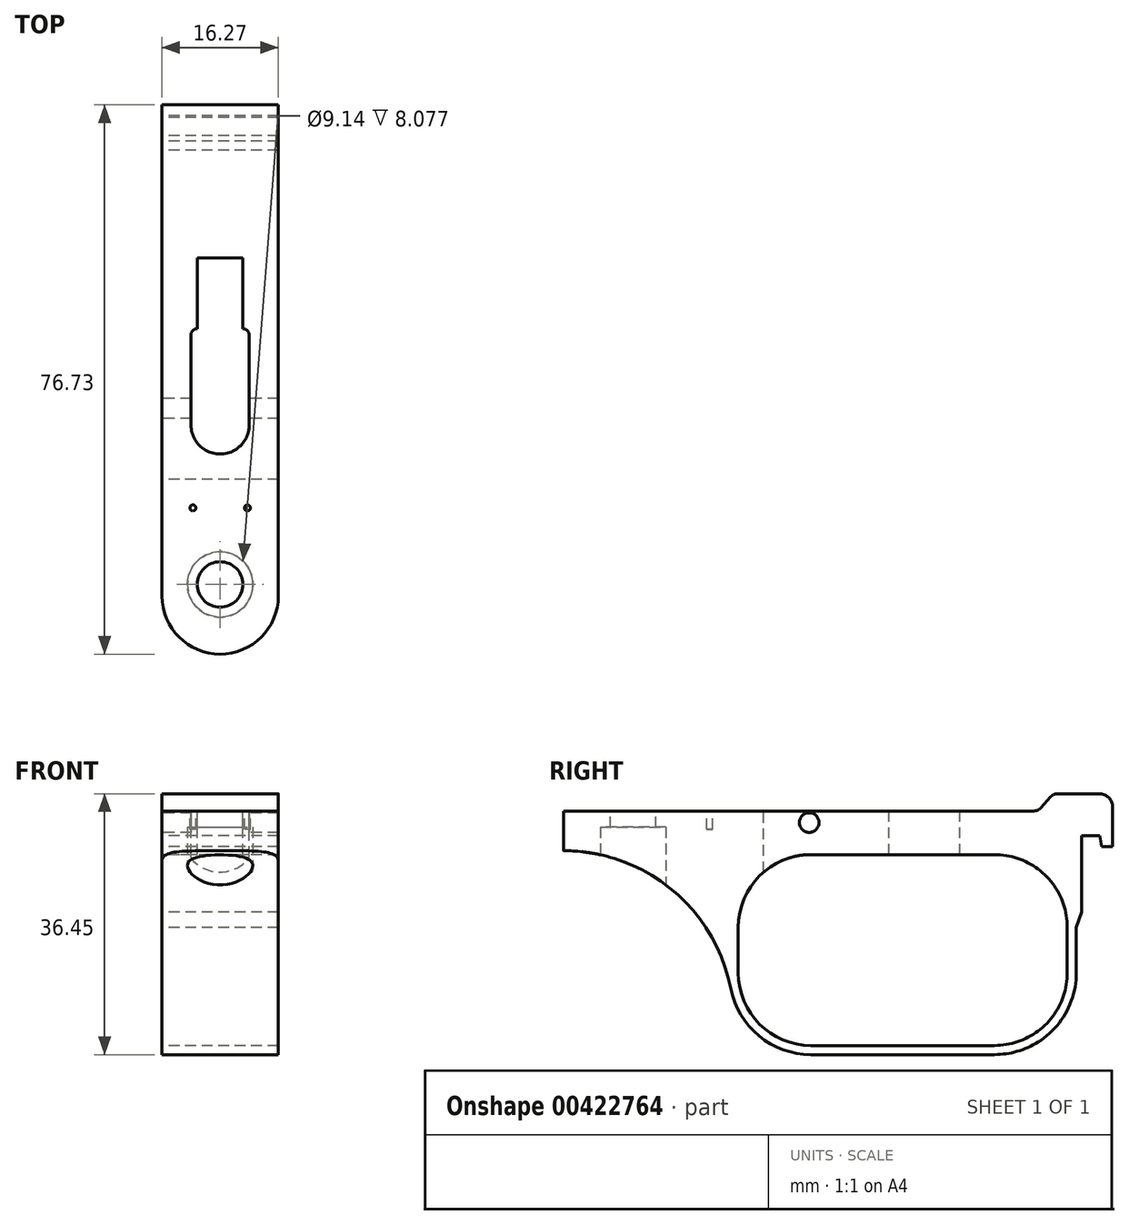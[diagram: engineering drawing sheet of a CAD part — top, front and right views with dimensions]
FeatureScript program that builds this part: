
annotation { "Feature Type Name" : "Feature", "Feature Type Description" : "" }
export const myFeature = defineFeature(function(context is Context, id is Id, definition is map)
    precondition{}
    {
        {
            var Q0;
            Q0=qCreatedBy(makeId("Top.planeOp"),FACE);
            var sketch = newSketch(context, id + "F0", { "sketchPlane" : qUnion([Q0])});
            skArc(sketch, "E0", {"start": v(-8.13, -41.11) * mm, "mid": v(0, -49.24) * mm, "end": v(8.13, -41.11) * mm});
            skCircle(sketch, "E1", {"center": v(0, -39.51) * mm, "radius": 3.18 * mm});
            skLineSegment(sketch, "E2", {"start": v(-8.13, -31.26) * mm, "end": v(8.13, -31.26) * mm});
            skCircle(sketch, "E3", {"center": v(3.81, -28.82) * mm, "radius": 0.42 * mm});
            skCircle(sketch, "E4", {"center": v(-3.8, -28.82) * mm, "radius": 0.42 * mm});
            skLineSegment(sketch, "E5", {"start": v(-8.13, -41.11) * mm, "end": v(-8.13, -31.26) * mm});
            skLineSegment(sketch, "E6", {"start": v(8.13, -41.11) * mm, "end": v(8.13, -31.26) * mm});
            skLineSegment(sketch, "E7", {"start": v(8.13, 17.06) * mm, "end": v(8.13, -31.26) * mm});
            skLineSegment(sketch, "E8", {"start": v(8.13, 17.06) * mm, "end": v(8.14, 23.18) * mm});
            skLineSegment(sketch, "E9", {"start": v(8.14, 23.18) * mm, "end": v(8.14, 25.72) * mm});
            skLineSegment(sketch, "E10", {"start": v(8.14, 25.72) * mm, "end": v(8.14, 27.5) * mm});
            skLineSegment(sketch, "E11", {"start": v(8.13, 17.06) * mm, "end": v(-8.13, 17.1) * mm});
            skLineSegment(sketch, "E12", {"start": v(8.14, 23.18) * mm, "end": v(-8.13, 23.18) * mm});
            skLineSegment(sketch, "E13", {"start": v(8.14, 25.72) * mm, "end": v(-8.13, 25.72) * mm});
            skLineSegment(sketch, "E14", {"start": v(8.14, 27.5) * mm, "end": v(-8.13, 27.5) * mm});
            skLineSegment(sketch, "E15", {"start": v(-8.13, -31.26) * mm, "end": v(-8.13, 17.1) * mm});
            skLineSegment(sketch, "E16", {"start": v(-8.13, 17.1) * mm, "end": v(-8.13, 23.18) * mm});
            skLineSegment(sketch, "E17", {"start": v(-8.13, 23.18) * mm, "end": v(-8.13, 25.72) * mm});
            skLineSegment(sketch, "E18", {"start": v(-8.13, 25.72) * mm, "end": v(-8.13, 27.5) * mm});
            skArc(sketch, "E19.0.1.0", {"start": v(-4.06, -17.24) * mm, "mid": v(0, -21.3) * mm, "end": v(4.07, -17.23) * mm});
            skLineSegment(sketch, "E19.0.1.1", {"start": v(-4.07, -4.66) * mm, "end": v(-4.06, -17.24) * mm});
            skLineSegment(sketch, "E19.0.1.2", {"start": v(4.05, -4.66) * mm, "end": v(4.07, -17.23) * mm});
            skArc(sketch, "E19.0.1.3", {"start": v(-3.18, -3.77) * mm, "mid": v(-3.8, -4.03) * mm, "end": v(-4.07, -4.66) * mm});
            skLineSegment(sketch, "E19.0.1.4", {"start": v(-3.18, -3.77) * mm, "end": v(-3.18, 6.13) * mm});
            skArc(sketch, "E19.0.1.5", {"start": v(4.05, -4.66) * mm, "mid": v(3.8, -4.04) * mm, "end": v(3.17, -3.77) * mm});
            skLineSegment(sketch, "E19.0.1.6", {"start": v(3.17, -3.77) * mm, "end": v(3.17, 6.13) * mm});
            skLineSegment(sketch, "E19.0.1.7", {"start": v(3.17, 6.13) * mm, "end": v(-3.18, 6.13) * mm});
            skSolve(sketch);
        }
        {
            var Q0;
            Q0=makeQuery(id+"F0.imprint","IMPRINT",FACE,{"disambiguationData":[TD([[makeQuery(id+"F0.imprint","IMPRINT",EDGE,{"derivedFrom":sQuery(id+"F0.wireOp",EDGE,"E0")}),1.0]])]});
            var Q1;
            {var subQ0=sQuery(id+"F0.wireOp",EDGE,"787198dd-bca4-4525-862f-a25401c4d90f");Q1=makeQuery(id+"F0.imprint","IMPRINT",FACE,{"disambiguationData":[TD([[makeQuery(id+"F0.imprint","IMPRINT",EDGE,{"derivedFrom":subQ0}),-1.0]])]});}
            var Q2;
            {var subQ0=sQuery(id+"F0.wireOp",EDGE,"d4342492-76fe-4402-a7e5-8071a383ea67");Q2=makeQuery(id+"F0.imprint","IMPRINT",FACE,{"disambiguationData":[TD([[makeQuery(id+"F0.imprint","IMPRINT",EDGE,{"derivedFrom":subQ0}),1.0]])]});}
            var Q3;
            Q3=makeQuery(id+"F0.imprint","IMPRINT",FACE,{"disambiguationData":[TD([[makeQuery(id+"F0.imprint","IMPRINT",EDGE,{"derivedFrom":sQuery(id+"F0.wireOp",EDGE,"14f3fbc3-f7db-4fca-b2d8-4976d205a7d3")}),1.0]])]});
            var Q4;
            Q4=makeQuery(id+"F0.imprint","IMPRINT",FACE,{"disambiguationData":[TD([[makeQuery(id+"F0.imprint","IMPRINT",EDGE,{"derivedFrom":sQuery(id+"F0.wireOp",EDGE,"E1")}),1.0]])]});
            var Q5;
            Q5=makeQuery(id+"F0.imprint","IMPRINT",FACE,{"disambiguationData":[TD([[makeQuery(id+"F0.imprint","IMPRINT",EDGE,{"derivedFrom":sQuery(id+"F0.wireOp",EDGE,"14f3fbc3-f7db-4fca-b2d8-4976d205a7d3")}),-1.0]])]});
            var Q6;
            Q6=makeQuery(id+"F0.imprint","IMPRINT",FACE,{"disambiguationData":[TD([[makeQuery(id+"F0.imprint","IMPRINT",EDGE,{"derivedFrom":sQuery(id+"F0.wireOp",EDGE,"E4")}),1.0]])]});
            var Q7;
            Q7=makeQuery(id+"F0.imprint","IMPRINT",FACE,{"disambiguationData":[TD([[makeQuery(id+"F0.imprint","IMPRINT",EDGE,{"derivedFrom":sQuery(id+"F0.wireOp",EDGE,"E3")}),1.0]])]});
            var Q8;
            Q8=makeQuery(id+"F0.imprint","IMPRINT",FACE,{"disambiguationData":[TD([[makeQuery(id+"F0.imprint","IMPRINT",EDGE,{"derivedFrom":sQuery(id+"F0.wireOp",EDGE,"E8")}),1.0]])]});
            var Q9;
            Q9=makeQuery(id+"F0.imprint","IMPRINT",FACE,{"disambiguationData":[TD([[makeQuery(id+"F0.imprint","IMPRINT",EDGE,{"derivedFrom":sQuery(id+"F0.wireOp",EDGE,"E2")}),1.0]])]});
            var Q10;
            Q10=makeQuery(id+"F0.imprint","IMPRINT",FACE,{"disambiguationData":[TD([[makeQuery(id+"F0.imprint","IMPRINT",EDGE,{"derivedFrom":sQuery(id+"F0.wireOp",EDGE,"E19.0.1.0")}),1.0]])]});
            extrude(context, id + "F1", {"entities" : qUnion([Q0, Q1, Q2, Q3, Q4, Q5, Q6, Q7, Q8, Q9, Q10]), "oppositeDirection" : true, "depth" : 34.54 * mm, "offsetDistance" : 25.4 * mm});
        }
        {
            var Q0;
            Q0=makeQuery(id+"F0.imprint","IMPRINT",FACE,{"disambiguationData":[TD([[makeQuery(id+"F0.imprint","IMPRINT",EDGE,{"derivedFrom":sQuery(id+"F0.wireOp",EDGE,"E8")}),1.0]])]});
            var Q1;
            Q1=makeQuery(id+"F0.imprint","IMPRINT",FACE,{"disambiguationData":[TD([[makeQuery(id+"F0.imprint","IMPRINT",EDGE,{"derivedFrom":sQuery(id+"F0.wireOp",EDGE,"E9")}),1.0]])]});
            var Q2;
            Q2=makeQuery(id+"F0.imprint","IMPRINT",FACE,{"disambiguationData":[TD([[makeQuery(id+"F0.imprint","IMPRINT",EDGE,{"derivedFrom":sQuery(id+"F0.wireOp",EDGE,"E10")}),1.0]])]});
            extrude(context, id + "F2", {"entities" : qUnion([Q0, Q1, Q2]), "operationType" : NewBodyOperationType.ADD, "depth" : 2.41 * mm, "offsetDistance" : 25.4 * mm});
        }
        {
            var Q0;
            Q0=makeQuery(id+"F0.imprint","IMPRINT",FACE,{"disambiguationData":[TD([[makeQuery(id+"F0.imprint","IMPRINT",EDGE,{"derivedFrom":sQuery(id+"F0.wireOp",EDGE,"E10")}),1.0]])]});
            extrude(context, id + "F3", {"entities" : qUnion([Q0]), "operationType" : NewBodyOperationType.ADD, "oppositeDirection" : true, "depth" : 4.95 * mm, "offsetDistance" : 25.4 * mm});
        }
        {
            var Q0;
            Q0=makeQuery(id+"F0.imprint","IMPRINT",FACE,{"disambiguationData":[TD([[makeQuery(id+"F0.imprint","IMPRINT",EDGE,{"derivedFrom":sQuery(id+"F0.wireOp",EDGE,"d4342492-76fe-4402-a7e5-8071a383ea67")}),-1.0]])]});
            var Q1;
            Q1=makeQuery(id+"F0.imprint","IMPRINT",FACE,{"disambiguationData":[TD([[makeQuery(id+"F0.imprint","IMPRINT",EDGE,{"derivedFrom":sQuery(id+"F0.wireOp",EDGE,"E9")}),1.0]])]});
            extrude(context, id + "F4", {"entities" : qUnion([Q0, Q1]), "operationType" : NewBodyOperationType.ADD, "oppositeDirection" : true, "depth" : 3.43 * mm, "offsetDistance" : 25.4 * mm});
        }
        {
            var Q0;
            Q0=makeQuery(id+"F3.opExtrude","CAP_EDGE",EDGE,{"disambiguationData":[OSD([sQuery(id+"F0.wireOp",EDGE,"E13")])],"isStart":false});
            chamfer(context, id + "F5", {"entities" : qUnion([Q0]), "chamferType" : ChamferType.TWO_OFFSETS, "width1" : 0.25 * mm, "oppositeDirection" : false, "width2" : 1.52 * mm, "tangentPropagation" : true});
        }
        {
            var Q0;
            Q0=makeQuery(id+"F2.opExtrude","CAP_EDGE",EDGE,{"disambiguationData":[OSD([sQuery(id+"F0.wireOp",EDGE,"4851dd6c-9b33-465a-a96c-daf8107e06ed")])],"isStart":false});
            var Q1;
            Q1=makeQuery(id+"F2.opExtrude","CAP_EDGE",EDGE,{"disambiguationData":[OSD([sQuery(id+"F0.wireOp",EDGE,"E14")])],"isStart":false});
            fillet(context, id + "F6", {"entities" : qUnion([Q0, Q1]), "radius" : 1.9 * mm, "tangentPropagation" : true, "allowEdgeOverflow" : false});
        }
        {
            var Q0;
            Q0=makeQuery(id+"F2.opExtrude","CAP_EDGE",EDGE,{"disambiguationData":[OSD([sQuery(id+"F0.wireOp",EDGE,"7dc91bf6-54e8-47e1-96ad-06bf4c2fe70e")])],"isStart":false});
            var Q1;
            Q1=makeQuery(id+"F2.opExtrude","CAP_EDGE",EDGE,{"disambiguationData":[OSD([sQuery(id+"F0.wireOp",EDGE,"E11")])],"isStart":false});
            chamfer(context, id + "F7", {"entities" : qUnion([Q0, Q1]), "chamferType" : ChamferType.TWO_OFFSETS, "width1" : 2.41 * mm, "oppositeDirection" : false, "width2" : 2.16 * mm, "tangentPropagation" : true});
        }
        {
            var Q0;
            {var subQ0=sQuery(id+"F0.wireOp",EDGE,"E11");Q0=makeQuery(id+"F7.opChamfer","BLEND_EDGE",EDGE,{"blendedFrom":[makeQuery(id+"F2.opExtrude","CAP_EDGE",EDGE,{"disambiguationData":[OSD([subQ0])],"isStart":false}),makeQuery(id+"F2.opExtrude","CAP_FACE",FACE,{"disambiguationData":[OSD([sQuery(id+"F0.wireOp",EDGE,"E8"),sQuery(id+"F0.wireOp",EDGE,"E9"),sQuery(id+"F0.wireOp",EDGE,"E10"),subQ0,sQuery(id+"F0.wireOp",EDGE,"E14"),sQuery(id+"F0.wireOp",EDGE,"E16"),sQuery(id+"F0.wireOp",EDGE,"E17"),sQuery(id+"F0.wireOp",EDGE,"E18")])],"isStart":false})],"blendedInto":[makeQuery(id+"F2.opExtrude","CAP_FACE",FACE,{"disambiguationData":[OSD([sQuery(id+"F0.wireOp",EDGE,"E8"),sQuery(id+"F0.wireOp",EDGE,"E9"),sQuery(id+"F0.wireOp",EDGE,"E10"),subQ0,sQuery(id+"F0.wireOp",EDGE,"E14"),sQuery(id+"F0.wireOp",EDGE,"E16"),sQuery(id+"F0.wireOp",EDGE,"E17"),sQuery(id+"F0.wireOp",EDGE,"E18")])],"isStart":false})]});}
            fillet(context, id + "F8", {"entities" : qUnion([Q0]), "radius" : 1.27 * mm, "tangentPropagation" : true, "allowEdgeOverflow" : false});
        }
        {
            var Q0;
            Q0=makeQuery(id+"F7.opChamfer","BLEND_EDGE",EDGE,{"blendedFrom":[makeQuery(id+"F2.opExtrude","CAP_EDGE",EDGE,{"disambiguationData":[OSD([sQuery(id+"F0.wireOp",EDGE,"E11")])],"isStart":false}),makeQuery(id+"F1.opExtrude","CAP_FACE",FACE,{"disambiguationData":[OSD([sQuery(id+"F0.wireOp",EDGE,"E0"),sQuery(id+"F0.wireOp",EDGE,"E5"),sQuery(id+"F0.wireOp",EDGE,"E6"),sQuery(id+"F0.wireOp",EDGE,"E7"),sQuery(id+"F0.wireOp",EDGE,"E8"),sQuery(id+"F0.wireOp",EDGE,"E12"),sQuery(id+"F0.wireOp",EDGE,"E15"),sQuery(id+"F0.wireOp",EDGE,"E16")])],"isStart":true})],"blendedInto":[makeQuery(id+"F1.opExtrude","CAP_FACE",FACE,{"disambiguationData":[OSD([sQuery(id+"F0.wireOp",EDGE,"E0"),sQuery(id+"F0.wireOp",EDGE,"E5"),sQuery(id+"F0.wireOp",EDGE,"E6"),sQuery(id+"F0.wireOp",EDGE,"E7"),sQuery(id+"F0.wireOp",EDGE,"E8"),sQuery(id+"F0.wireOp",EDGE,"E12"),sQuery(id+"F0.wireOp",EDGE,"E15"),sQuery(id+"F0.wireOp",EDGE,"E16")])],"isStart":true})]});
            fillet(context, id + "F9", {"entities" : qUnion([Q0]), "radius" : 1.27 * mm, "tangentPropagation" : true, "allowEdgeOverflow" : false});
        }
        {
            var Q0;
            {var subQ0=sQuery(id+"F0.wireOp",EDGE,"E17");var subQ1=sQuery(id+"F0.wireOp",EDGE,"E18");var subQ2=sQuery(id+"F0.wireOp",EDGE,"E16");Q0=makeQuery(id+"F4.boolean.opBoolean","MERGE",FACE,{"derivedFrom":[makeQuery(id+"F3.boolean.opBoolean","MERGE",FACE,{"derivedFrom":[makeQuery(id+"F2.boolean.opBoolean","MERGE",FACE,{"derivedFrom":[makeQuery(id+"F1.opExtrude","SWEPT_FACE",FACE,{"disambiguationData":[OSD([sQuery(id+"F0.wireOp",EDGE,"E15"),subQ2])]}),makeQuery(id+"F2.opExtrude","SWEPT_FACE",FACE,{"disambiguationData":[OSD([subQ2,subQ0,subQ1])]})]}),makeQuery(id+"F3.opExtrude","SWEPT_FACE",FACE,{"disambiguationData":[OSD([subQ1])]})]}),makeQuery(id+"F4.opExtrude","SWEPT_FACE",FACE,{"disambiguationData":[OSD([subQ0])]})]});}
            var sketch = newSketch(context, id + "F10", { "sketchPlane" : qUnion([Q0])});
            skCircle(sketch, "E20.1.0.20", {"center": v(14.92, -1.63) * mm, "radius": 1.37 * mm});
            skLineSegment(sketch, "E21.0.1.2", {"start": v(26.1, -5.56) * mm, "end": v(55.09, -5.56) * mm});
            skArc(sketch, "E21.0.1.5", {"start": v(14.67, -34.04) * mm, "mid": v(22.75, -30.69) * mm, "end": v(26.1, -22.6) * mm});
            skLineSegment(sketch, "E21.0.1.6", {"start": v(14.67, -34.04) * mm, "end": v(-10.98, -34.04) * mm});
            skLineSegment(sketch, "E21.0.1.7", {"start": v(-23.18, -34.54) * mm, "end": v(55.09, -34.54) * mm});
            skLineSegment(sketch, "E21.0.1.8", {"start": v(-10.98, -32.77) * mm, "end": v(14.67, -32.77) * mm});
            skArc(sketch, "E21.0.1.9", {"start": v(24.83, -22.6) * mm, "mid": v(21.85, -29.8) * mm, "end": v(14.67, -32.77) * mm});
            skLineSegment(sketch, "E21.0.1.10", {"start": v(24.83, -16.26) * mm, "end": v(24.83, -22.6) * mm});
            skArc(sketch, "E21.0.1.11", {"start": v(14.67, -6.1) * mm, "mid": v(21.85, -9.07) * mm, "end": v(24.83, -16.26) * mm});
            skLineSegment(sketch, "E21.0.1.12", {"start": v(14.67, -6.1) * mm, "end": v(-10.98, -6.1) * mm});
            skArc(sketch, "E21.0.1.13", {"start": v(-10.98, -6.1) * mm, "mid": v(-18.17, -9.07) * mm, "end": v(-21.14, -16.26) * mm});
            skLineSegment(sketch, "E21.0.1.14", {"start": v(-21.14, -16.26) * mm, "end": v(-21.14, -22.6) * mm});
            skArc(sketch, "E21.0.1.15", {"start": v(-21.14, -22.6) * mm, "mid": v(-18.17, -29.8) * mm, "end": v(-10.98, -32.77) * mm});
            skArc(sketch, "E21.0.1.16", {"start": v(-22.41, -22.6) * mm, "mid": v(-19.07, -30.69) * mm, "end": v(-10.98, -34.04) * mm});
            skLineSegment(sketch, "E21.0.1.17", {"start": v(-23.18, -14.1) * mm, "end": v(-23.18, -34.54) * mm});
            skLineSegment(sketch, "E21.0.1.18", {"start": v(-22.41, -16.26) * mm, "end": v(-22.41, -22.6) * mm});
            skLineSegment(sketch, "E21.0.1.19", {"start": v(-23.18, -14.1) * mm, "end": v(-22.41, -16.26) * mm});
            skLineSegment(sketch, "E22", {"start": v(55.09, -5.56) * mm, "end": v(55.09, -34.54) * mm});
            skLineSegment(sketch, "E23", {"start": v(26.1, -5.56) * mm, "end": v(26.1, -22.6) * mm});
            skSolve(sketch);
        }
        {
            var Q0;
            Q0=qSketchRegion(id+"F10",true);
            extrude(context, id + "F11", {"entities" : qUnion([Q0]), "operationType" : NewBodyOperationType.REMOVE, "endBound" : BoundingType.THROUGH_ALL, "oppositeDirection" : true, "depth" : 25.4 * mm, "offsetDistance" : 25.4 * mm});
        }
        {
            var Q0;
            Q0=makeQuery(id+"F0.imprint","IMPRINT",FACE,{"disambiguationData":[TD([[makeQuery(id+"F0.imprint","IMPRINT",EDGE,{"derivedFrom":sQuery(id+"F0.wireOp",EDGE,"E1")}),1.0]])]});
            extrude(context, id + "F12", {"entities" : qUnion([Q0]), "operationType" : NewBodyOperationType.REMOVE, "endBound" : BoundingType.THROUGH_ALL, "oppositeDirection" : true, "depth" : 25.4 * mm, "offsetDistance" : 25.4 * mm});
        }
        {
            var Q0;
            Q0=makeQuery(id+"F0.imprint","IMPRINT",FACE,{"disambiguationData":[TD([[makeQuery(id+"F0.imprint","IMPRINT",EDGE,{"derivedFrom":sQuery(id+"F0.wireOp",EDGE,"14f3fbc3-f7db-4fca-b2d8-4976d205a7d3")}),1.0]])]});
            var Q1;
            Q1=makeQuery(id+"F0.imprint","IMPRINT",FACE,{"disambiguationData":[TD([[makeQuery(id+"F0.imprint","IMPRINT",EDGE,{"derivedFrom":sQuery(id+"F0.wireOp",EDGE,"E19.0.1.0")}),1.0]])]});
            extrude(context, id + "F13", {"entities" : qUnion([Q0, Q1]), "operationType" : NewBodyOperationType.REMOVE, "oppositeDirection" : true, "depth" : 8.9 * mm, "offsetDistance" : 25.4 * mm});
        }
        {
            var Q0;
            Q0=makeQuery(id+"F0.imprint","IMPRINT",FACE,{"disambiguationData":[TD([[makeQuery(id+"F0.imprint","IMPRINT",EDGE,{"derivedFrom":sQuery(id+"F0.wireOp",EDGE,"E4")}),1.0]])]});
            var Q1;
            Q1=makeQuery(id+"F0.imprint","IMPRINT",FACE,{"disambiguationData":[TD([[makeQuery(id+"F0.imprint","IMPRINT",EDGE,{"derivedFrom":sQuery(id+"F0.wireOp",EDGE,"E3")}),1.0]])]});
            extrude(context, id + "F14", {"entities" : qUnion([Q0, Q1]), "operationType" : NewBodyOperationType.REMOVE, "oppositeDirection" : true, "depth" : 2.54 * mm, "offsetDistance" : 25.4 * mm});
        }
        {
            var Q0;
            Q0=makeQuery(id+"F11.boolean.opBoolean","COPY",FACE,{"derivedFrom":makeQuery(id+"F11.opExtrude","SWEPT_FACE",FACE,{"disambiguationData":[OSD([sQuery(id+"F10.wireOp",EDGE,"E21.0.1.2")])]})});
            var sketch = newSketch(context, id + "F15", { "sketchPlane" : qUnion([Q0])});
            skCircle(sketch, "E24", {"center": v(0, 39.51) * mm, "radius": 4.57 * mm});
            skSolve(sketch);
        }
        {
            var Q0;
            Q0=makeQuery(id+"F15.imprint","IMPRINT",FACE,{"disambiguationData":[TD([[makeQuery(id+"F15.imprint","IMPRINT",EDGE,{"derivedFrom":sQuery(id+"F15.wireOp",EDGE,"E24")}),1.0]])]});
            extrude(context, id + "F16", {"entities" : qUnion([Q0]), "operationType" : NewBodyOperationType.REMOVE, "oppositeDirection" : true, "depth" : 3.3 * mm, "offsetDistance" : 25.4 * mm});
        }
        {
            var Q0;
            Q0=makeQuery(id+"F11.boolean.opBoolean","COPY",EDGE,{"derivedFrom":makeQuery(id+"F11.opExtrude","SWEPT_EDGE",EDGE,{"disambiguationData":[OSD([sQuery(id+"F10.wireOp",EDGE,"E21.0.1.2"),sQuery(id+"F10.wireOp",EDGE,"E23")])]})});
            fillet(context, id + "F17", {"entities" : qUnion([Q0]), "radius" : 23.79 * mm, "tangentPropagation" : true, "allowEdgeOverflow" : false});
        }
    });
